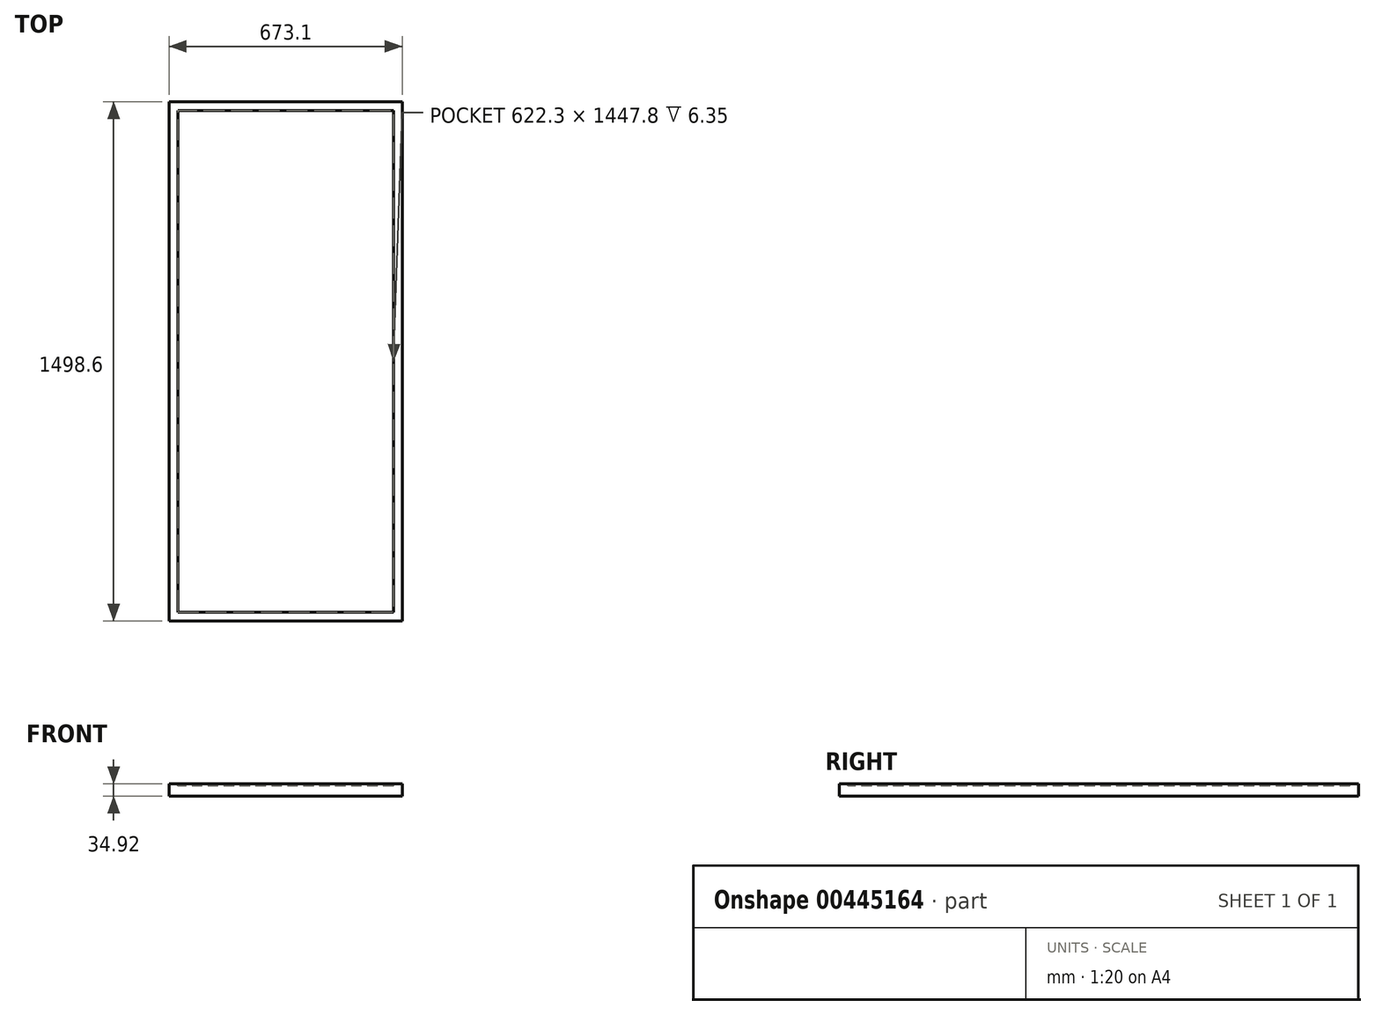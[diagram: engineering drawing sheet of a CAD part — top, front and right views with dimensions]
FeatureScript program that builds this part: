
annotation { "Feature Type Name" : "Feature", "Feature Type Description" : "" }
export const myFeature = defineFeature(function(context is Context, id is Id, definition is map)
    precondition{}
    {
        {
            var Q0;
            Q0=qCreatedBy(makeId("Top.planeOp"),FACE);
            var sketch = newSketch(context, id + "F0", { "sketchPlane" : qUnion([Q0])});
            skLineSegment(sketch, "E0.bottom", {"start": v(0, 1498.6) * mm, "end": v(673.1, 1498.6) * mm});
            skLineSegment(sketch, "E0.top", {"start": v(0, 0) * mm, "end": v(673.1, 0) * mm});
            skLineSegment(sketch, "E0.left", {"start": v(0, 1498.6) * mm, "end": v(0, 0) * mm});
            skLineSegment(sketch, "E0.right", {"start": v(673.1, 1498.6) * mm, "end": v(673.1, 0) * mm});
            skSolve(sketch);
        }
        {
            var Q0;
            Q0=makeQuery(id+"F0.imprint","IMPRINT",FACE,{"disambiguationData":[TD([[makeQuery(id+"F0.imprint","IMPRINT",EDGE,{"derivedFrom":sQuery(id+"F0.wireOp",EDGE,"E0.bottom")}),-1.0]])]});
            extrude(context, id + "F1", {"entities" : qUnion([Q0]), "depth" : 34.92 * mm});
        }
        {
            var Q0;
            Q0=makeQuery(id+"F1.opExtrude","CAP_FACE",FACE,{"disambiguationData":[OSD([sQuery(id+"F0.wireOp",EDGE,"E0.bottom"),sQuery(id+"F0.wireOp",EDGE,"E0.top"),sQuery(id+"F0.wireOp",EDGE,"E0.left"),sQuery(id+"F0.wireOp",EDGE,"E0.right")])],"isStart":false});
            var sketch = newSketch(context, id + "F2", { "sketchPlane" : qUnion([Q0])});
            skLineSegment(sketch, "E1.0", {"start": v(25.4, 1473.2) * mm, "end": v(25.4, 25.4) * mm});
            skLineSegment(sketch, "E1.1", {"start": v(647.7, 1473.2) * mm, "end": v(25.4, 1473.2) * mm});
            skLineSegment(sketch, "E1.2", {"start": v(647.7, 25.4) * mm, "end": v(647.7, 1473.2) * mm});
            skLineSegment(sketch, "E1.3", {"start": v(25.4, 25.4) * mm, "end": v(647.7, 25.4) * mm});
            skSolve(sketch);
        }
        {
            var Q0;
            Q0 = qSketchRegion(id + "F2", true);
            extrude(context, id + "F3", {"entities" : qUnion([Q0]), "operationType" : NewBodyOperationType.REMOVE, "oppositeDirection" : true, "depth" : 6.35 * mm});
        }
    });
